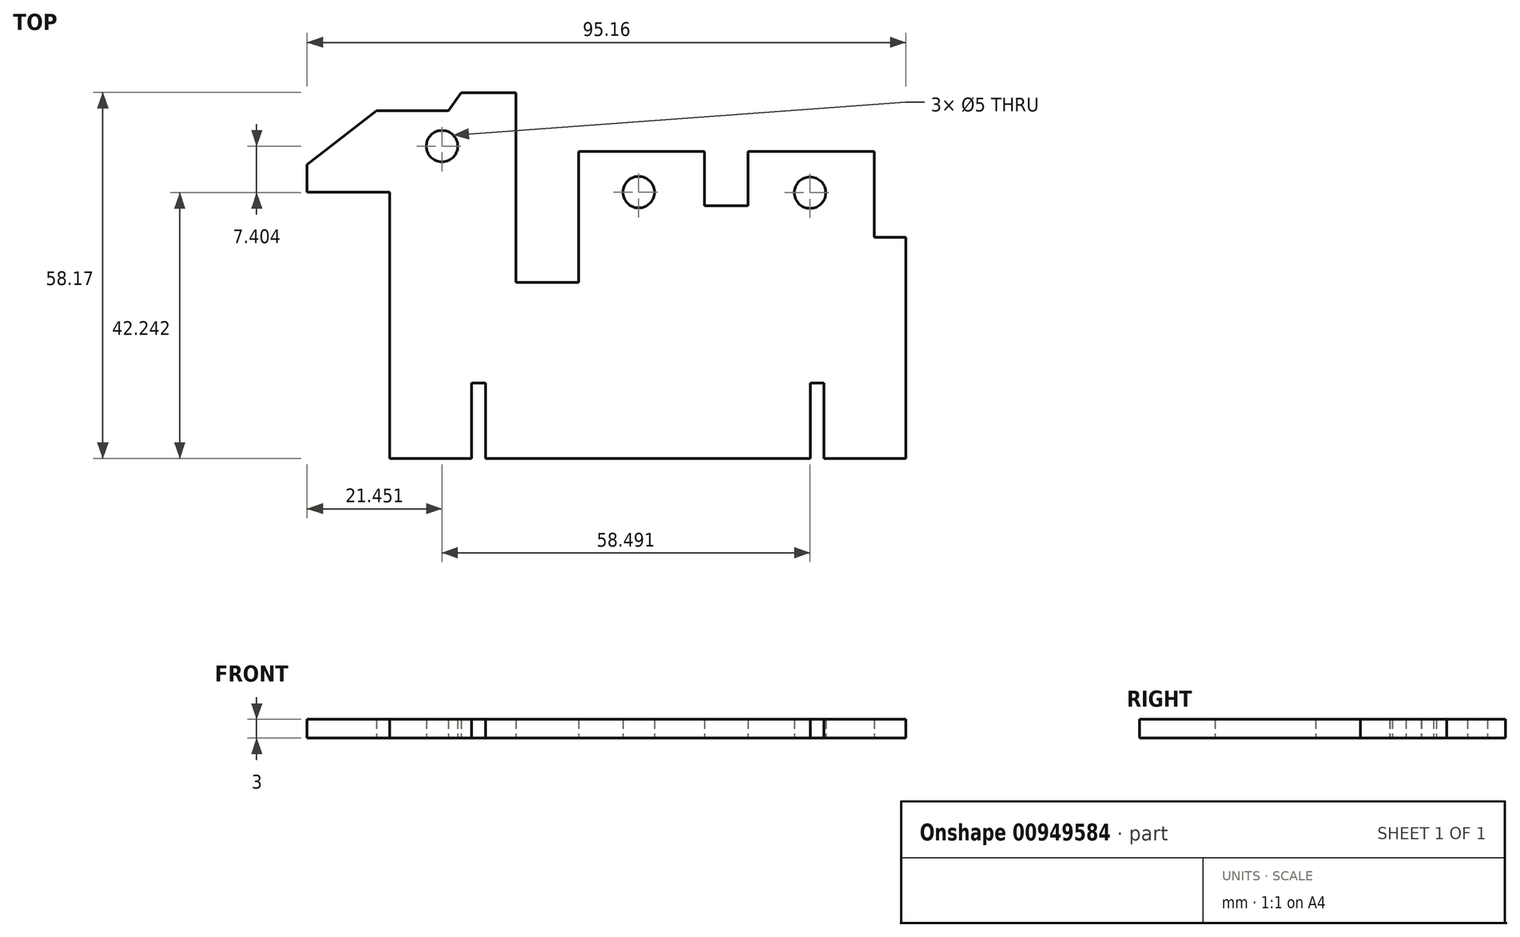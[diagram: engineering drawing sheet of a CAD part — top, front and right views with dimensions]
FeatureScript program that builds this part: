
annotation { "Feature Type Name" : "Feature", "Feature Type Description" : "" }
export const myFeature = defineFeature(function(context is Context, id is Id, definition is map)
    precondition{}
    {
        {
            var Q0;
            Q0=qCreatedBy(makeId("Top.planeOp"),FACE);
            var sketch = newSketch(context, id + "F0", { "sketchPlane" : qUnion([Q0])});
            skLineSegment(sketch, "E0", {"start": v(-39.55, -20.48) * mm, "end": v(-26.55, -20.48) * mm});
            skLineSegment(sketch, "E1", {"start": v(-26.55, -20.48) * mm, "end": v(-26.55, -8.5) * mm});
            skLineSegment(sketch, "E2", {"start": v(-26.55, -8.5) * mm, "end": v(-24.37, -8.5) * mm});
            skLineSegment(sketch, "E3", {"start": v(-24.37, -8.5) * mm, "end": v(-24.37, -20.48) * mm});
            skLineSegment(sketch, "E4", {"start": v(-24.37, -20.48) * mm, "end": v(27.27, -20.48) * mm});
            skLineSegment(sketch, "E5", {"start": v(27.27, -20.48) * mm, "end": v(27.27, -8.5) * mm});
            skLineSegment(sketch, "E6", {"start": v(27.27, -8.5) * mm, "end": v(29.44, -8.5) * mm});
            skLineSegment(sketch, "E7", {"start": v(29.44, -8.5) * mm, "end": v(29.44, -20.48) * mm});
            skLineSegment(sketch, "E8", {"start": v(29.44, -20.48) * mm, "end": v(42.45, -20.48) * mm});
            skLineSegment(sketch, "E9", {"start": v(42.45, -20.48) * mm, "end": v(42.45, 14.66) * mm});
            skLineSegment(sketch, "E10", {"start": v(42.45, 14.66) * mm, "end": v(37.47, 14.66) * mm});
            skLineSegment(sketch, "E11", {"start": v(37.47, 14.66) * mm, "end": v(37.47, 28.33) * mm});
            skLineSegment(sketch, "E12", {"start": v(37.47, 28.33) * mm, "end": v(17.37, 28.33) * mm});
            skLineSegment(sketch, "E13", {"start": v(17.37, 28.33) * mm, "end": v(17.37, 19.7) * mm});
            skLineSegment(sketch, "E14", {"start": v(17.37, 19.7) * mm, "end": v(10.45, 19.7) * mm});
            skLineSegment(sketch, "E15", {"start": v(10.45, 19.7) * mm, "end": v(10.45, 28.33) * mm});
            skLineSegment(sketch, "E16", {"start": v(10.45, 28.33) * mm, "end": v(-9.57, 28.33) * mm});
            skLineSegment(sketch, "E17", {"start": v(-9.57, 28.33) * mm, "end": v(-9.57, 7.52) * mm});
            skLineSegment(sketch, "E18", {"start": v(-9.57, 7.52) * mm, "end": v(-19.54, 7.52) * mm});
            skLineSegment(sketch, "E19", {"start": v(-19.54, 7.52) * mm, "end": v(-19.54, 37.69) * mm});
            skLineSegment(sketch, "E20", {"start": v(-19.54, 37.69) * mm, "end": v(-28.2, 37.69) * mm});
            skLineSegment(sketch, "E21", {"start": v(-28.2, 37.69) * mm, "end": v(-30.25, 34.82) * mm});
            skLineSegment(sketch, "E22", {"start": v(-30.25, 34.82) * mm, "end": v(-41.69, 34.82) * mm});
            skLineSegment(sketch, "E23", {"start": v(-41.69, 34.82) * mm, "end": v(-52.7, 26.25) * mm});
            skLineSegment(sketch, "E24", {"start": v(-52.7, 26.25) * mm, "end": v(-52.7, 21.85) * mm});
            skLineSegment(sketch, "E25", {"start": v(-52.7, 21.85) * mm, "end": v(-39.56, 21.85) * mm});
            skLineSegment(sketch, "E26", {"start": v(-39.56, 21.85) * mm, "end": v(-39.55, -20.48) * mm});
            skCircle(sketch, "E27", {"center": v(0, 21.85) * mm, "radius": 2.5 * mm});
            skCircle(sketch, "E28", {"center": v(27.23, 21.76) * mm, "radius": 2.5 * mm});
            skCircle(sketch, "E29", {"center": v(-31.26, 29.17) * mm, "radius": 2.5 * mm});
            skSolve(sketch);
        }
        {
            var Q0;
            Q0=makeQuery(id+"F0.imprint","IMPRINT",FACE,{"disambiguationData":[TD([[makeQuery(id+"F0.imprint","IMPRINT",EDGE,{"derivedFrom":sQuery(id+"F0.wireOp",EDGE,"E0")}),1.0]])]});
            extrude(context, id + "F1", {"entities" : qUnion([Q0]), "depth" : 3 * mm, "offsetDistance" : 25 * mm});
        }
    });
